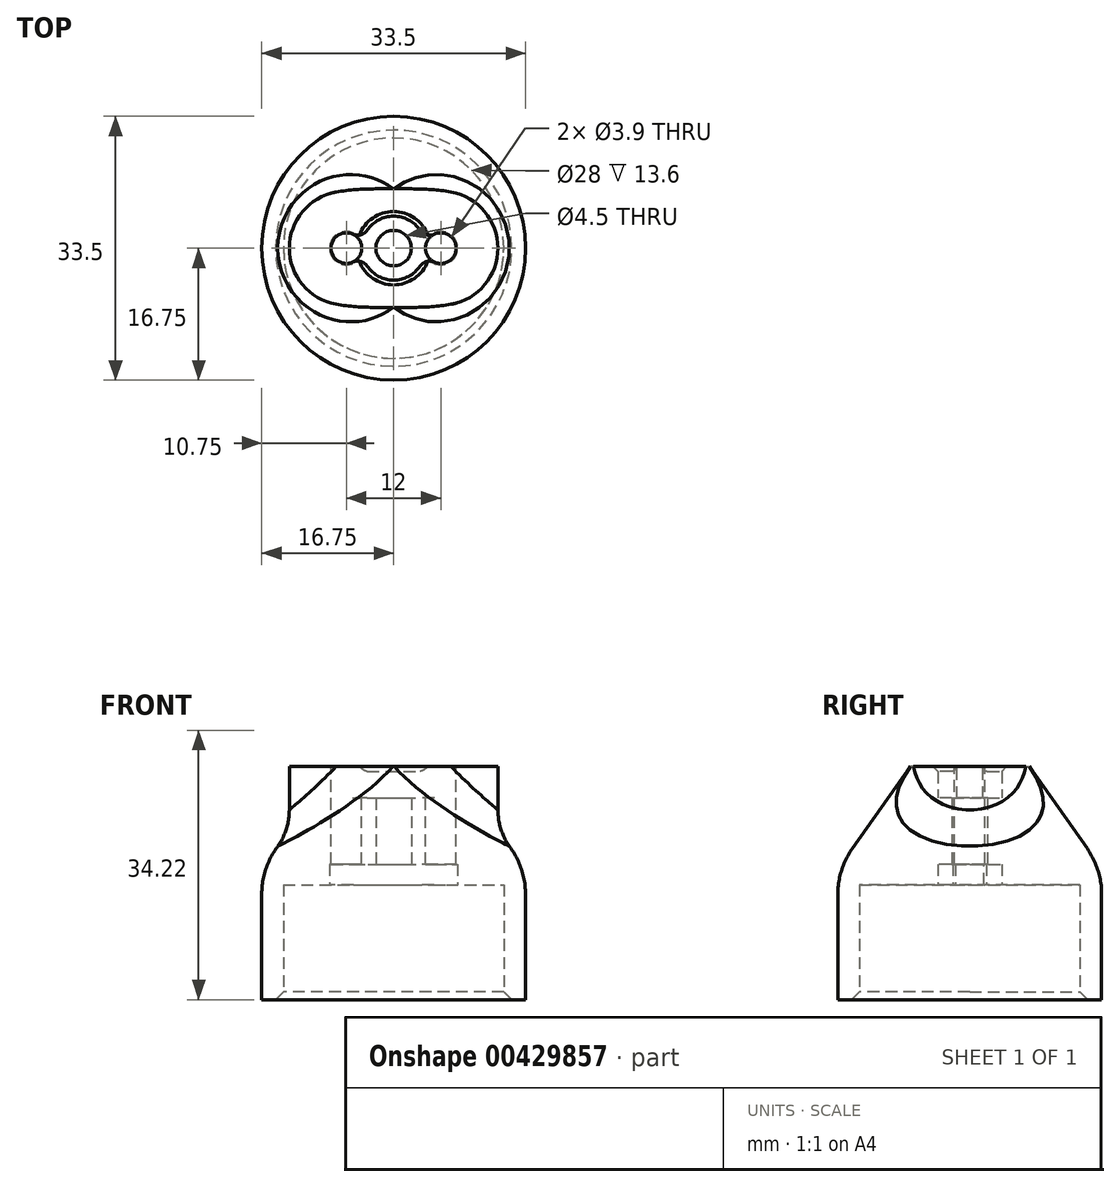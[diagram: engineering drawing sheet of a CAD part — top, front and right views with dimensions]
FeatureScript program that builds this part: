
annotation { "Feature Type Name" : "Feature", "Feature Type Description" : "" }
export const myFeature = defineFeature(function(context is Context, id is Id, definition is map)
    precondition{}
    {
        {
            var Q0;
            Q0=qCreatedBy(makeId("Front.planeOp"),FACE);
            var sketch = newSketch(context, id + "F0", { "sketchPlane" : qUnion([Q0])});
            skLineSegment(sketch, "E0", {"start": v(-14, 0) * mm, "end": v(-14, 14.6) * mm});
            skLineSegment(sketch, "E1", {"start": v(-14, 14.6) * mm, "end": v(-4.06, 14.6) * mm});
            skLineSegment(sketch, "E2", {"start": v(-4.06, 14.6) * mm, "end": v(-4.06, 29.6) * mm});
            skLineSegment(sketch, "E3", {"start": v(-4.06, 29.6) * mm, "end": v(-6.06, 29.6) * mm});
            skLineSegment(sketch, "E4", {"start": v(-6.06, 29.6) * mm, "end": v(-6.06, 16.6) * mm});
            skLineSegment(sketch, "E5", {"start": v(-6.06, 16.6) * mm, "end": v(-16.75, 16.6) * mm});
            skLineSegment(sketch, "E6", {"start": v(-16.75, 16.6) * mm, "end": v(-16.75, 0) * mm});
            skLineSegment(sketch, "E7", {"start": v(-16.75, 0) * mm, "end": v(-14, 0) * mm});
            skPoint(sketch, "E8.visualSharp", {"position": v(-14, 14.6) * mm});
            skPoint(sketch, "E9.visualSharp", {"position": v(-6.06, 16.6) * mm});
            skPoint(sketch, "E10.visualSharp", {"position": v(-16.75, 16.6) * mm});
            skLineSegment(sketch, "E11", {"start": v(0, -7.55) * mm, "end": v(0, 0) * mm});
            skLineSegment(sketch, "E12", {"start": v(-4.06, 25.6) * mm, "end": v(-2.25, 25.6) * mm});
            skLineSegment(sketch, "E13", {"start": v(-2.25, 25.6) * mm, "end": v(-2.25, 17.2) * mm});
            skLineSegment(sketch, "E14", {"start": v(-2.25, 17.2) * mm, "end": v(-4.06, 17.2) * mm});
            skLineSegment(sketch, "E15", {"start": v(-6.06, 29.6) * mm, "end": v(-7.56, 29.6) * mm});
            skLineSegment(sketch, "E16", {"start": v(-16.75, 16.6) * mm, "end": v(-7.56, 29.6) * mm});
            skSolve(sketch);
        }
        {
            var Q0;
            {var subQ0=sQuery(id+"F0.wireOp",EDGE,"E12");Q0=makeQuery(id+"F0.imprint","IMPRINT",FACE,{"disambiguationData":[TD([[makeQuery(id+"F0.imprint","IMPRINT",EDGE,{"derivedFrom":subQ0}),-1.0]])]});}
            var Q1;
            {var subQ4=sQuery(id+"F0.wireOp",EDGE,"E0");Q1=makeQuery(id+"F0.imprint","IMPRINT",FACE,{"disambiguationData":[TD([[makeQuery(id+"F0.imprint","IMPRINT",EDGE,{"derivedFrom":subQ4}),1.0]])]});}
            var Q2;
            {var subQ0=sQuery(id+"F0.wireOp",EDGE,"BeAn98SS-8YNr-UEEg-DAqC-0HcXDUS5vDmL");Q2=makeQuery(id+"F0.imprint","IMPRINT",FACE,{"disambiguationData":[TD([[makeQuery(id+"F0.imprint","IMPRINT",EDGE,{"derivedFrom":subQ0}),1.0]])]});}
            var Q3;
            Q3=makeQuery(id+"F0.imprint","IMPRINT",FACE,{"disambiguationData":[TD([[makeQuery(id+"F0.imprint","IMPRINT",EDGE,{"derivedFrom":sQuery(id+"F0.wireOp",EDGE,"E4")}),-1.0]])]});
            var Q4;
            Q4=sQuery(id+"F0.wireOp",EDGE,"E11");
            revolve(context, id + "F1", {"surfaceOperationType" : NewSurfaceOperationType.NEW, "entities" : qUnion([Q0, Q1, Q2, Q3]), "axis" : qUnion([Q4]), "revolveType" : RevolveType.FULL});
        }
        {
            var Q0;
            Q0=makeQuery(id+"F1.opRevolve","SWEPT_EDGE",EDGE,{"disambiguationData":[OSD([sQuery(id+"F0.wireOp",EDGE,"E0"),sQuery(id+"F0.wireOp",EDGE,"E7")])]});
            chamfer(context, id + "F2", {"entities" : qUnion([Q0]), "width" : 1 * mm, "tangentPropagation" : true});
        }
        {
            var Q0;
            Q0=makeQuery(id+"F1.opRevolve","SWEPT_EDGE",EDGE,{"disambiguationData":[OSD([sQuery(id+"F0.wireOp",EDGE,"E2"),sQuery(id+"F0.wireOp",EDGE,"E3")])]});
            chamfer(context, id + "F3", {"entities" : qUnion([Q0]), "width" : .6 * mm, "tangentPropagation" : true});
        }
        {
            var Q0;
            Q0=makeQuery(id+"F1.opRevolve","SWEPT_EDGE",EDGE,{"disambiguationData":[OSD([sQuery(id+"F0.wireOp",EDGE,"E5"),sQuery(id+"F0.wireOp",EDGE,"E6")])]});
            var Q1;
            Q1=makeQuery(id+"F1.opRevolve","SWEPT_EDGE",EDGE,{"disambiguationData":[OSD([sQuery(id+"F0.wireOp",EDGE,"E5"),sQuery(id+"F0.wireOp",EDGE,"j4Ist1vo-cUh0-sd4F-eBGg-UatqZb88we41")])]});
            fillet(context, id + "F4", {"entities" : qUnion([Q0, Q1]), "radius" : 10 * mm, "tangentPropagation" : true, "allowEdgeOverflow" : false});
        }
        {
            var Q0;
            Q0=makeQuery(id+"F1.opRevolve","SWEPT_FACE",FACE,{"disambiguationData":[OSD([sQuery(id+"F0.wireOp",EDGE,"E3")])]});
            var sketch = newSketch(context, id + "F5", { "sketchPlane" : qUnion([Q0])});
            skLineSegment(sketch, "E17.bottom", {"start": v(6, 7.25) * mm, "end": v(-6, 7.25) * mm});
            skLineSegment(sketch, "E17.top", {"start": v(6, -7.25) * mm, "end": v(-6, -7.25) * mm});
            skLineSegment(sketch, "E17.left", {"start": v(6, 7.25) * mm, "end": v(6, -7.25) * mm, "construction": true});
            skLineSegment(sketch, "E17.right", {"start": v(-6, 7.25) * mm, "end": v(-6, -7.25) * mm, "construction": true});
            skPoint(sketch, "E17.middle", {"position": v(0, 0) * mm});
            skArc(sketch, "E18", {"start": v(-6, 7.25) * mm, "mid": v(-13.25, 0) * mm, "end": v(-6, -7.25) * mm});
            skArc(sketch, "E19", {"start": v(6, -7.25) * mm, "mid": v(13.25, 0) * mm, "end": v(6, 7.25) * mm});
            skCircle(sketch, "E20", {"center": v(-6, 0) * mm, "radius": 1.95 * mm});
            skCircle(sketch, "E21", {"center": v(6, 0) * mm, "radius": 1.95 * mm});
            skSolve(sketch);
        }
        {
            var Q0;
            {var subQ4=sQuery(id+"F5.wireOp",EDGE,"E18");Q0=makeQuery(id+"F5.imprint","IMPRINT",FACE,{"disambiguationData":[TD([[makeQuery(id+"F5.imprint","IMPRINT",EDGE,{"derivedFrom":subQ4}),1.0]])]});}
            var Q1;
            {var subQ0=sQuery(id+"F5.wireOp",EDGE,"E19");Q1=makeQuery(id+"F5.imprint","IMPRINT",FACE,{"disambiguationData":[TD([[makeQuery(id+"F5.imprint","IMPRINT",EDGE,{"derivedFrom":subQ0}),1.0]])]});}
            extrude(context, id + "F6", {"entities" : qUnion([Q0, Q1]), "operationType" : NewBodyOperationType.ADD, "endBound" : BoundingType.UP_TO_NEXT, "oppositeDirection" : true, "depth" : 25 * mm, "offsetDistance" : 25 * mm});
        }
        {
            var Q0;
            {var subQ0=sQuery(id+"F5.wireOp",EDGE,"E20");var subQ1=sQuery(id+"F0.wireOp",EDGE,"E15");var subQ2=makeQuery(id+"F1.opRevolve","SWEPT_EDGE",EDGE,{"disambiguationData":[OSD([subQ1,sQuery(id+"F0.wireOp",EDGE,"E16")])]});var subQ3=makeQuery(id+"F5.imprint","INTERSECT",VERTEX,{"disambiguationData":[OD(0.0)],"derivedFrom":[subQ2,subQ0]});Q0=makeQuery(id+"F5.imprint","IMPRINT",FACE,{"disambiguationData":[TD([[makeQuery(id+"F5.imprint","IMPRINT",EDGE,{"disambiguationData":[TD([[subQ3,1.0]])],"derivedFrom":subQ2}),-1.0]])]});}
            var Q1;
            {var subQ0=sQuery(id+"F5.wireOp",EDGE,"E20");var subQ1=makeQuery(id+"F1.opRevolve","SWEPT_EDGE",EDGE,{"disambiguationData":[OSD([sQuery(id+"F0.wireOp",EDGE,"E15"),sQuery(id+"F0.wireOp",EDGE,"E16")])]});var subQ2=makeQuery(id+"F5.imprint","INTERSECT",VERTEX,{"disambiguationData":[OD(0.0)],"derivedFrom":[subQ1,subQ0]});Q1=makeQuery(id+"F5.imprint","IMPRINT",FACE,{"disambiguationData":[TD([[makeQuery(id+"F5.imprint","IMPRINT",EDGE,{"disambiguationData":[TD([[subQ2,-1.0]])],"derivedFrom":subQ0}),1.0]])]});}
            var Q2;
            {var subQ0=sQuery(id+"F5.wireOp",EDGE,"E20");var subQ1=sQuery(id+"F0.wireOp",EDGE,"E3");var subQ2=makeQuery(id+"F3.opChamfer","BLEND_EDGE",EDGE,{"blendedFrom":[makeQuery(id+"F1.opRevolve","SWEPT_EDGE",EDGE,{"disambiguationData":[OSD([sQuery(id+"F0.wireOp",EDGE,"E2"),subQ1])]}),makeQuery(id+"F1.opRevolve","SWEPT_FACE",FACE,{"disambiguationData":[OSD([subQ1,sQuery(id+"F0.wireOp",EDGE,"E15")])]})],"blendedInto":[makeQuery(id+"F1.opRevolve","SWEPT_FACE",FACE,{"disambiguationData":[OSD([subQ1,sQuery(id+"F0.wireOp",EDGE,"E15")])]})]});var subQ3=makeQuery(id+"F5.imprint","INTERSECT",VERTEX,{"disambiguationData":[OD(0.0)],"derivedFrom":[subQ2,subQ0]});Q2=makeQuery(id+"F5.imprint","IMPRINT",FACE,{"disambiguationData":[TD([[makeQuery(id+"F5.imprint","IMPRINT",EDGE,{"disambiguationData":[TD([[subQ3,1.0]])],"derivedFrom":subQ0}),1.0]])]});}
            var Q3;
            {var subQ0=sQuery(id+"F5.wireOp",EDGE,"E21");var subQ1=sQuery(id+"F0.wireOp",EDGE,"E3");var subQ2=makeQuery(id+"F3.opChamfer","BLEND_EDGE",EDGE,{"blendedFrom":[makeQuery(id+"F1.opRevolve","SWEPT_EDGE",EDGE,{"disambiguationData":[OSD([sQuery(id+"F0.wireOp",EDGE,"E2"),subQ1])]}),makeQuery(id+"F1.opRevolve","SWEPT_FACE",FACE,{"disambiguationData":[OSD([subQ1,sQuery(id+"F0.wireOp",EDGE,"E15")])]})],"blendedInto":[makeQuery(id+"F1.opRevolve","SWEPT_FACE",FACE,{"disambiguationData":[OSD([subQ1,sQuery(id+"F0.wireOp",EDGE,"E15")])]})]});var subQ3=makeQuery(id+"F5.imprint","INTERSECT",VERTEX,{"disambiguationData":[OD(0.0)],"derivedFrom":[subQ2,subQ0]});Q3=makeQuery(id+"F5.imprint","IMPRINT",FACE,{"disambiguationData":[TD([[makeQuery(id+"F5.imprint","IMPRINT",EDGE,{"disambiguationData":[TD([[subQ3,-1.0]])],"derivedFrom":subQ0}),1.0]])]});}
            var Q4;
            {var subQ0=sQuery(id+"F5.wireOp",EDGE,"E21");var subQ1=sQuery(id+"F0.wireOp",EDGE,"E15");var subQ5=makeQuery(id+"F1.opRevolve","SWEPT_EDGE",EDGE,{"disambiguationData":[OSD([subQ1,sQuery(id+"F0.wireOp",EDGE,"E16")])]});var subQ6=makeQuery(id+"F5.imprint","INTERSECT",VERTEX,{"disambiguationData":[OD(0.0)],"derivedFrom":[subQ5,subQ0]});Q4=makeQuery(id+"F5.imprint","IMPRINT",FACE,{"disambiguationData":[TD([[makeQuery(id+"F5.imprint","IMPRINT",EDGE,{"disambiguationData":[TD([[subQ6,-1.0]])],"derivedFrom":subQ5}),-1.0]])]});}
            var Q5;
            {var subQ0=sQuery(id+"F5.wireOp",EDGE,"E21");var subQ1=makeQuery(id+"F1.opRevolve","SWEPT_EDGE",EDGE,{"disambiguationData":[OSD([sQuery(id+"F0.wireOp",EDGE,"E15"),sQuery(id+"F0.wireOp",EDGE,"E16")])]});var subQ2=makeQuery(id+"F5.imprint","INTERSECT",VERTEX,{"disambiguationData":[OD(0.0)],"derivedFrom":[subQ1,subQ0]});Q5=makeQuery(id+"F5.imprint","IMPRINT",FACE,{"disambiguationData":[TD([[makeQuery(id+"F5.imprint","IMPRINT",EDGE,{"disambiguationData":[TD([[subQ2,1.0]])],"derivedFrom":subQ0}),1.0]])]});}
            extrude(context, id + "F7", {"entities" : qUnion([Q0, Q1, Q2, Q3, Q4, Q5]), "operationType" : NewBodyOperationType.REMOVE, "oppositeDirection" : true, "depth" : 25 * mm, "offsetDistance" : 25 * mm});
        }
        {
            var Q0;
            Q0=makeQuery(id+"F1.opRevolve","SWEPT_FACE",FACE,{"disambiguationData":[OSD([sQuery(id+"F0.wireOp",EDGE,"E1")])]});
            var sketch = newSketch(context, id + "F8", { "sketchPlane" : qUnion([Q0])});
            skCircle(sketch, "E22", {"center": v(-6, 0) * mm, "radius": 2.12 * mm});
            skCircle(sketch, "E23", {"center": v(6, 0) * mm, "radius": 2.12 * mm});
            skSolve(sketch);
        }
        {
            var Q0;
            Q0=makeQuery(id+"F6.opExtrude","CAP_EDGE",EDGE,{"disambiguationData":[OSD([sQuery(id+"F5.wireOp",EDGE,"E19")])],"isStart":false});
            var Q1;
            Q1=makeQuery(id+"F6.opExtrude","CAP_EDGE",EDGE,{"disambiguationData":[OSD([sQuery(id+"F5.wireOp",EDGE,"E18")])],"isStart":false});
            fillet(context, id + "F9", {"entities" : qUnion([Q0, Q1]), "radius" : 8 * mm, "tangentPropagation" : true, "allowEdgeOverflow" : false});
        }
        {
            var Q0;
            {var subQ1=sQuery(id+"F0.wireOp",EDGE,"E1");Q0=makeQuery(id+"F8.imprint","IMPRINT",FACE,{"disambiguationData":[TD([[makeQuery(id+"F8.imprint","IMPRINT",EDGE,{"derivedFrom":makeQuery(id+"F7.boolean.opBoolean","INTERSECT",EDGE,{"derivedFrom":[makeQuery(id+"F1.opRevolve","SWEPT_FACE",FACE,{"disambiguationData":[OSD([subQ1])]}),makeQuery(id+"F7.opExtrude","SWEPT_FACE",FACE,{"disambiguationData":[OSD([sQuery(id+"F5.wireOp",EDGE,"E20")])]})]})}),1.0]])]});}
            var Q1;
            {var subQ0=sQuery(id+"F8.wireOp",EDGE,"E22");var subQ1=makeQuery(id+"F1.opRevolve","SWEPT_EDGE",EDGE,{"disambiguationData":[OSD([sQuery(id+"F0.wireOp",EDGE,"E1"),sQuery(id+"F0.wireOp",EDGE,"x58vAvJs-wTtj-4foS-Q0Mj-Vjn6i8wRsJp5")])]});var subQ2=makeQuery(id+"F8.imprint","INTERSECT",VERTEX,{"disambiguationData":[OD(0.0)],"derivedFrom":[subQ1,subQ0]});Q1=makeQuery(id+"F8.imprint","IMPRINT",FACE,{"disambiguationData":[TD([[makeQuery(id+"F8.imprint","IMPRINT",EDGE,{"disambiguationData":[TD([[subQ2,1.0]])],"derivedFrom":subQ0}),1.0]])]});}
            var Q2;
            {var subQ0=sQuery(id+"F8.wireOp",EDGE,"E23");var subQ1=makeQuery(id+"F1.opRevolve","SWEPT_EDGE",EDGE,{"disambiguationData":[OSD([sQuery(id+"F0.wireOp",EDGE,"E1"),sQuery(id+"F0.wireOp",EDGE,"x58vAvJs-wTtj-4foS-Q0Mj-Vjn6i8wRsJp5")])]});var subQ2=makeQuery(id+"F8.imprint","INTERSECT",VERTEX,{"disambiguationData":[OD(0.0)],"derivedFrom":[subQ1,subQ0]});Q2=makeQuery(id+"F8.imprint","IMPRINT",FACE,{"disambiguationData":[TD([[makeQuery(id+"F8.imprint","IMPRINT",EDGE,{"disambiguationData":[TD([[subQ2,-1.0]])],"derivedFrom":subQ0}),1.0]])]});}
            var Q3;
            {var subQ1=sQuery(id+"F0.wireOp",EDGE,"E1");Q3=makeQuery(id+"F8.imprint","IMPRINT",FACE,{"disambiguationData":[TD([[makeQuery(id+"F8.imprint","IMPRINT",EDGE,{"derivedFrom":makeQuery(id+"F7.boolean.opBoolean","INTERSECT",EDGE,{"derivedFrom":[makeQuery(id+"F1.opRevolve","SWEPT_FACE",FACE,{"disambiguationData":[OSD([subQ1])]}),makeQuery(id+"F7.opExtrude","SWEPT_FACE",FACE,{"disambiguationData":[OSD([sQuery(id+"F5.wireOp",EDGE,"E21")])]})]})}),1.0]])]});}
            extrude(context, id + "F10", {"entities" : qUnion([Q0, Q1, Q2, Q3]), "operationType" : NewBodyOperationType.REMOVE, "endBound" : BoundingType.SYMMETRIC, "oppositeDirection" : true, "depth" : 5.2 * mm, "offsetDistance" : 25 * mm});
        }
        {
            var Q0;
            {var subQ0=sQuery(id+"F0.wireOp",EDGE,"E2");Q0=makeQuery(id+"F7.boolean.opBoolean","INTERSECT",EDGE,{"disambiguationData":[OD(1.0)],"derivedFrom":[makeQuery(id+"F1.opRevolve","SWEPT_FACE",FACE,{"disambiguationData":[OSD([subQ0]),TDD([makeQuery(id+"F0.imprint","IMPRINT",EDGE,{"disambiguationData":[TD([[makeQuery(id+"F0.imprint","INTERSECT",VERTEX,{"derivedFrom":[subQ0,sQuery(id+"F0.wireOp",EDGE,"E3")]}),1.0]])],"derivedFrom":subQ0})])]}),makeQuery(id+"F7.opExtrude","SWEPT_FACE",FACE,{"disambiguationData":[OSD([sQuery(id+"F5.wireOp",EDGE,"E20")])]})]});}
            var Q1;
            {var subQ0=sQuery(id+"F0.wireOp",EDGE,"E2");Q1=makeQuery(id+"F7.boolean.opBoolean","INTERSECT",EDGE,{"disambiguationData":[OD(1.0)],"derivedFrom":[makeQuery(id+"F1.opRevolve","SWEPT_FACE",FACE,{"disambiguationData":[OSD([subQ0]),TDD([makeQuery(id+"F0.imprint","IMPRINT",EDGE,{"disambiguationData":[TD([[makeQuery(id+"F0.imprint","INTERSECT",VERTEX,{"derivedFrom":[subQ0,sQuery(id+"F0.wireOp",EDGE,"E3")]}),1.0]])],"derivedFrom":subQ0})])]}),makeQuery(id+"F7.opExtrude","SWEPT_FACE",FACE,{"disambiguationData":[OSD([sQuery(id+"F5.wireOp",EDGE,"E21")])]})]});}
            var Q2;
            {var subQ0=sQuery(id+"F0.wireOp",EDGE,"E2");Q2=makeQuery(id+"F7.boolean.opBoolean","INTERSECT",EDGE,{"disambiguationData":[OD(0.0)],"derivedFrom":[makeQuery(id+"F1.opRevolve","SWEPT_FACE",FACE,{"disambiguationData":[OSD([subQ0]),TDD([makeQuery(id+"F0.imprint","IMPRINT",EDGE,{"disambiguationData":[TD([[makeQuery(id+"F0.imprint","INTERSECT",VERTEX,{"derivedFrom":[subQ0,sQuery(id+"F0.wireOp",EDGE,"E3")]}),1.0]])],"derivedFrom":subQ0})])]}),makeQuery(id+"F7.opExtrude","SWEPT_FACE",FACE,{"disambiguationData":[OSD([sQuery(id+"F5.wireOp",EDGE,"E21")])]})]});}
            var Q3;
            {var subQ0=sQuery(id+"F0.wireOp",EDGE,"E2");Q3=makeQuery(id+"F7.boolean.opBoolean","INTERSECT",EDGE,{"disambiguationData":[OD(0.0)],"derivedFrom":[makeQuery(id+"F1.opRevolve","SWEPT_FACE",FACE,{"disambiguationData":[OSD([subQ0]),TDD([makeQuery(id+"F0.imprint","IMPRINT",EDGE,{"disambiguationData":[TD([[makeQuery(id+"F0.imprint","INTERSECT",VERTEX,{"derivedFrom":[subQ0,sQuery(id+"F0.wireOp",EDGE,"E3")]}),1.0]])],"derivedFrom":subQ0})])]}),makeQuery(id+"F7.opExtrude","SWEPT_FACE",FACE,{"disambiguationData":[OSD([sQuery(id+"F5.wireOp",EDGE,"E20")])]})]});}
            fillet(context, id + "F11", {"entities" : qUnion([Q0, Q1, Q2, Q3]), "radius" : 1.5 * mm, "tangentPropagation" : true, "allowEdgeOverflow" : false});
        }
        {
            var Q0;
            {var subQ0=sQuery(id+"F0.wireOp",EDGE,"E2");Q0=makeQuery(id+"F10.boolean.opBoolean","INTERSECT",EDGE,{"derivedFrom":[makeQuery(id+"F7.boolean.opBoolean","SPLIT",FACE,{"disambiguationData":[OD(1.0)],"derivedFrom":makeQuery(id+"F1.opRevolve","SWEPT_FACE",FACE,{"disambiguationData":[OSD([subQ0]),TDD([makeQuery(id+"F0.imprint","IMPRINT",EDGE,{"disambiguationData":[TD([[makeQuery(id+"F0.imprint","INTERSECT",VERTEX,{"derivedFrom":[sQuery(id+"F0.wireOp",EDGE,"E1"),subQ0]}),-1.0]])],"derivedFrom":subQ0})])]})}),makeQuery(id+"F10.opExtrude","SWEPT_FACE",FACE,{"disambiguationData":[OSD([sQuery(id+"F8.wireOp",EDGE,"E22")])]})]});}
            var Q1;
            {var subQ0=sQuery(id+"F0.wireOp",EDGE,"E2");Q1=makeQuery(id+"F10.boolean.opBoolean","INTERSECT",EDGE,{"derivedFrom":[makeQuery(id+"F7.boolean.opBoolean","SPLIT",FACE,{"disambiguationData":[OD(0.0)],"derivedFrom":makeQuery(id+"F1.opRevolve","SWEPT_FACE",FACE,{"disambiguationData":[OSD([subQ0]),TDD([makeQuery(id+"F0.imprint","IMPRINT",EDGE,{"disambiguationData":[TD([[makeQuery(id+"F0.imprint","INTERSECT",VERTEX,{"derivedFrom":[sQuery(id+"F0.wireOp",EDGE,"E1"),subQ0]}),-1.0]])],"derivedFrom":subQ0})])]})}),makeQuery(id+"F10.opExtrude","SWEPT_FACE",FACE,{"disambiguationData":[OSD([sQuery(id+"F8.wireOp",EDGE,"E22")])]})]});}
            var Q2;
            {var subQ0=sQuery(id+"F0.wireOp",EDGE,"E2");Q2=makeQuery(id+"F10.boolean.opBoolean","INTERSECT",EDGE,{"derivedFrom":[makeQuery(id+"F7.boolean.opBoolean","SPLIT",FACE,{"disambiguationData":[OD(1.0)],"derivedFrom":makeQuery(id+"F1.opRevolve","SWEPT_FACE",FACE,{"disambiguationData":[OSD([subQ0]),TDD([makeQuery(id+"F0.imprint","IMPRINT",EDGE,{"disambiguationData":[TD([[makeQuery(id+"F0.imprint","INTERSECT",VERTEX,{"derivedFrom":[sQuery(id+"F0.wireOp",EDGE,"E1"),subQ0]}),-1.0]])],"derivedFrom":subQ0})])]})}),makeQuery(id+"F10.opExtrude","SWEPT_FACE",FACE,{"disambiguationData":[OSD([sQuery(id+"F8.wireOp",EDGE,"E23")])]})]});}
            var Q3;
            {var subQ0=sQuery(id+"F0.wireOp",EDGE,"E2");Q3=makeQuery(id+"F10.boolean.opBoolean","INTERSECT",EDGE,{"derivedFrom":[makeQuery(id+"F7.boolean.opBoolean","SPLIT",FACE,{"disambiguationData":[OD(0.0)],"derivedFrom":makeQuery(id+"F1.opRevolve","SWEPT_FACE",FACE,{"disambiguationData":[OSD([subQ0]),TDD([makeQuery(id+"F0.imprint","IMPRINT",EDGE,{"disambiguationData":[TD([[makeQuery(id+"F0.imprint","INTERSECT",VERTEX,{"derivedFrom":[sQuery(id+"F0.wireOp",EDGE,"E1"),subQ0]}),-1.0]])],"derivedFrom":subQ0})])]})}),makeQuery(id+"F10.opExtrude","SWEPT_FACE",FACE,{"disambiguationData":[OSD([sQuery(id+"F8.wireOp",EDGE,"E23")])]})]});}
            fillet(context, id + "F12", {"entities" : qUnion([Q0, Q1, Q2, Q3]), "radius" : 1.5 * mm, "tangentPropagation" : true, "allowEdgeOverflow" : false});
        }
    });
